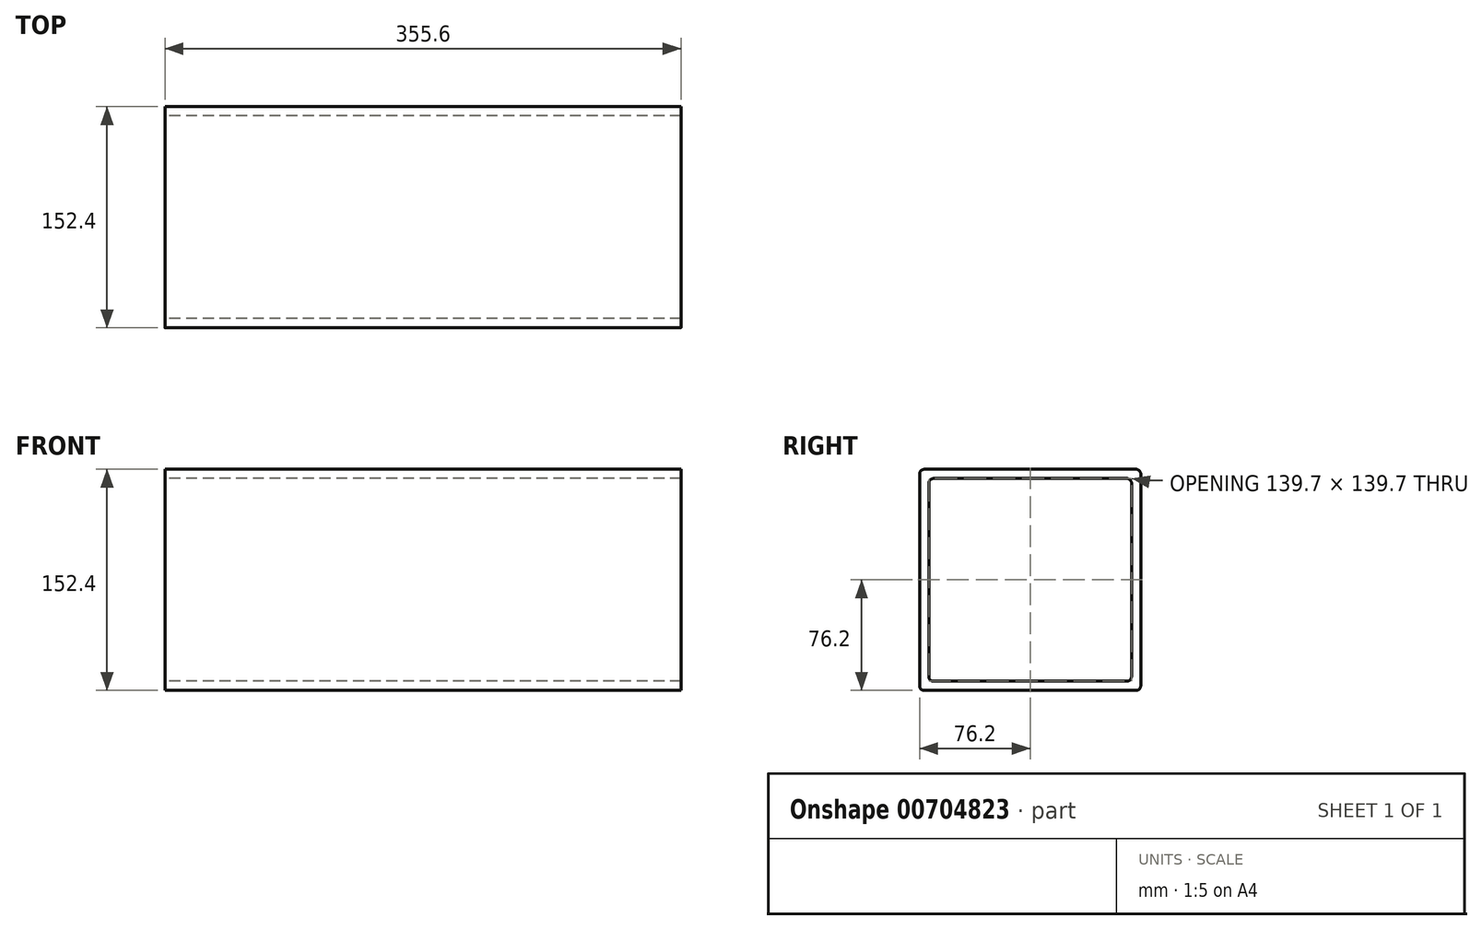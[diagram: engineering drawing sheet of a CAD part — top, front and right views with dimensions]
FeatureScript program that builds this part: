
annotation { "Feature Type Name" : "Feature", "Feature Type Description" : "" }
export const myFeature = defineFeature(function(context is Context, id is Id, definition is map)
    precondition{}
    {
        {
            var Q0;
            Q0=qCreatedBy(makeId("Right.planeOp"),FACE);
            var sketch = newSketch(context, id + "F0", { "sketchPlane" : qUnion([Q0])});
            skLineSegment(sketch, "E0.bottom", {"start": v(-73.03, 76.2) * mm, "end": v(73.03, 76.2) * mm});
            skLineSegment(sketch, "E0.top", {"start": v(-73.03, -76.2) * mm, "end": v(73.02, -76.2) * mm});
            skLineSegment(sketch, "E0.left", {"start": v(-76.2, 73.02) * mm, "end": v(-76.2, -73.03) * mm});
            skLineSegment(sketch, "E0.right", {"start": v(76.2, 73.02) * mm, "end": v(76.2, -73.03) * mm});
            skPoint(sketch, "E0.middle", {"position": v(0, 0) * mm});
            skLineSegment(sketch, "E1.0", {"start": v(-69.85, 66.68) * mm, "end": v(-69.85, -66.67) * mm});
            skLineSegment(sketch, "E2.3", {"start": v(-66.68, -69.85) * mm, "end": v(66.68, -69.85) * mm});
            skLineSegment(sketch, "E3.0", {"start": v(69.85, 66.68) * mm, "end": v(69.85, -66.67) * mm});
            skLineSegment(sketch, "E3.1", {"start": v(-66.68, 69.85) * mm, "end": v(66.68, 69.85) * mm});
            skPoint(sketch, "E4.visualSharp", {"position": v(-76.2, 76.2) * mm});
            skArc(sketch, "E4.filletArc", {"start": v(-73.03, 76.2) * mm, "mid": v(-75.27, 75.27) * mm, "end": v(-76.2, 73.02) * mm});
            skPoint(sketch, "E5.visualSharp", {"position": v(76.2, 76.2) * mm});
            skArc(sketch, "E5.filletArc", {"start": v(76.2, 73.02) * mm, "mid": v(75.27, 75.27) * mm, "end": v(73.03, 76.2) * mm});
            skPoint(sketch, "E6.visualSharp", {"position": v(76.2, -76.2) * mm});
            skArc(sketch, "E6.filletArc", {"start": v(73.02, -76.2) * mm, "mid": v(75.27, -75.27) * mm, "end": v(76.2, -73.03) * mm});
            skPoint(sketch, "E7.visualSharp", {"position": v(-76.2, -76.2) * mm});
            skArc(sketch, "E7.filletArc", {"start": v(-76.2, -73.03) * mm, "mid": v(-75.27, -75.27) * mm, "end": v(-73.03, -76.2) * mm});
            skPoint(sketch, "E8.visualSharp", {"position": v(-69.85, -69.85) * mm});
            skArc(sketch, "E8.filletArc", {"start": v(-69.85, -66.67) * mm, "mid": v(-68.92, -68.92) * mm, "end": v(-66.68, -69.85) * mm});
            skPoint(sketch, "E9.visualSharp", {"position": v(-69.85, 69.85) * mm});
            skArc(sketch, "E9.filletArc", {"start": v(-66.68, 69.85) * mm, "mid": v(-68.92, 68.92) * mm, "end": v(-69.85, 66.68) * mm});
            skPoint(sketch, "E10.visualSharp", {"position": v(69.85, 69.85) * mm});
            skArc(sketch, "E10.filletArc", {"start": v(69.85, 66.68) * mm, "mid": v(68.92, 68.92) * mm, "end": v(66.68, 69.85) * mm});
            skPoint(sketch, "E11.visualSharp", {"position": v(69.85, -69.85) * mm});
            skArc(sketch, "E11.filletArc", {"start": v(66.68, -69.85) * mm, "mid": v(68.92, -68.92) * mm, "end": v(69.85, -66.67) * mm});
            skSolve(sketch);
        }
        {
            var Q0;
            Q0=makeQuery(id+"F0.imprint","IMPRINT",FACE,{"disambiguationData":[TD([[makeQuery(id+"F0.imprint","IMPRINT",EDGE,{"derivedFrom":sQuery(id+"F0.wireOp",EDGE,"E0.bottom")}),-1.0]])]});
            extrude(context, id + "F1", {"entities" : qUnion([Q0]), "depth" : 355.6 * mm, "offsetDistance" : 25.4 * mm});
        }
    });
